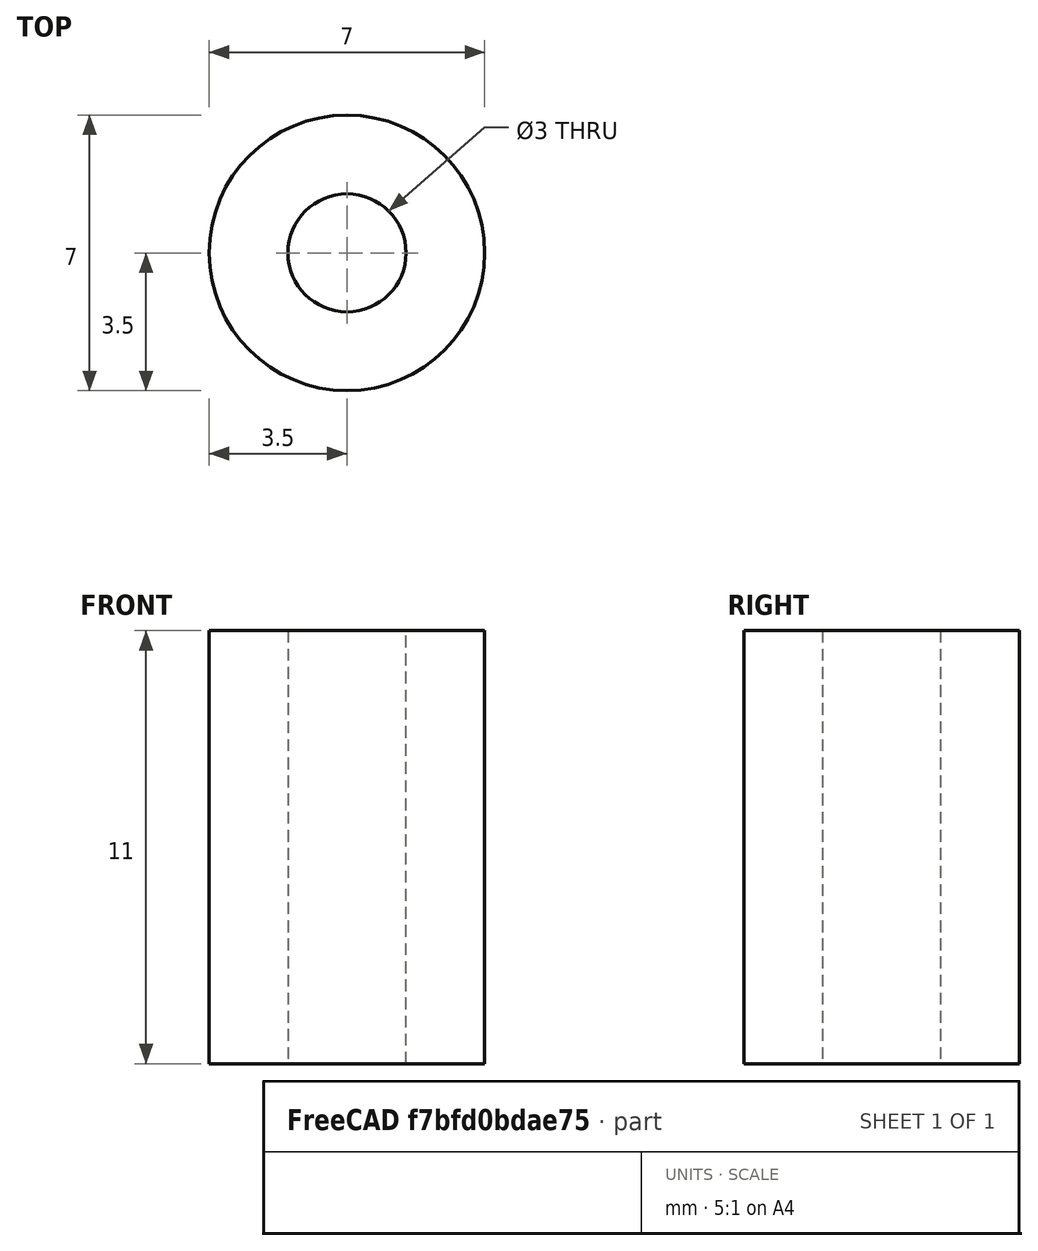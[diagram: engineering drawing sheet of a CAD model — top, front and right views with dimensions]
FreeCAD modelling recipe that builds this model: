
FCSTD DOCUMENT  (FreeCAD 0.19R19180 (Git))
Label: standoffs
License: All rights reserved
LicenseURL: http://en.wikipedia.org/wiki/All_rights_reserved
objects: Sketcher::SketchObject×1, PartDesign::Pad×1, PartDesign::Body×1
note: 4 computed .brp shape members not serialized (recipe doc carries the construction recipe); baked Part::Feature solids carry a one-line shape summary decoded from their .brp

FEATURE [Sketcher::SketchObject] Sketch
  MapMode = 5
  Support = -> [XY_Plane]
  sketch-geometry (2):
    g0: Circle CenterX=0 CenterY=0 CenterZ=0 NormalX=0 NormalY=0 NormalZ=1 AngleXU=0 Radius=3.5
    g1: Circle CenterX=0 CenterY=0 CenterZ=0 NormalX=0 NormalY=0 NormalZ=1 AngleXU=0 Radius=1.5
  constraints (4):
    c: Coincident(g0,g-1)
    c: Coincident(g1,g0)
    c: Diameter(g1) = 3
    c: Diameter(g0) = 7
FEATURE [PartDesign::Pad] Pad
  Length = 11
  Length2 = 100
  Profile = -> Sketch
  Type = 0
FEATURE [PartDesign::Body] Body
  Group = -> [Sketch,Pad]
  Origin = -> Origin
  Tip = -> Pad
